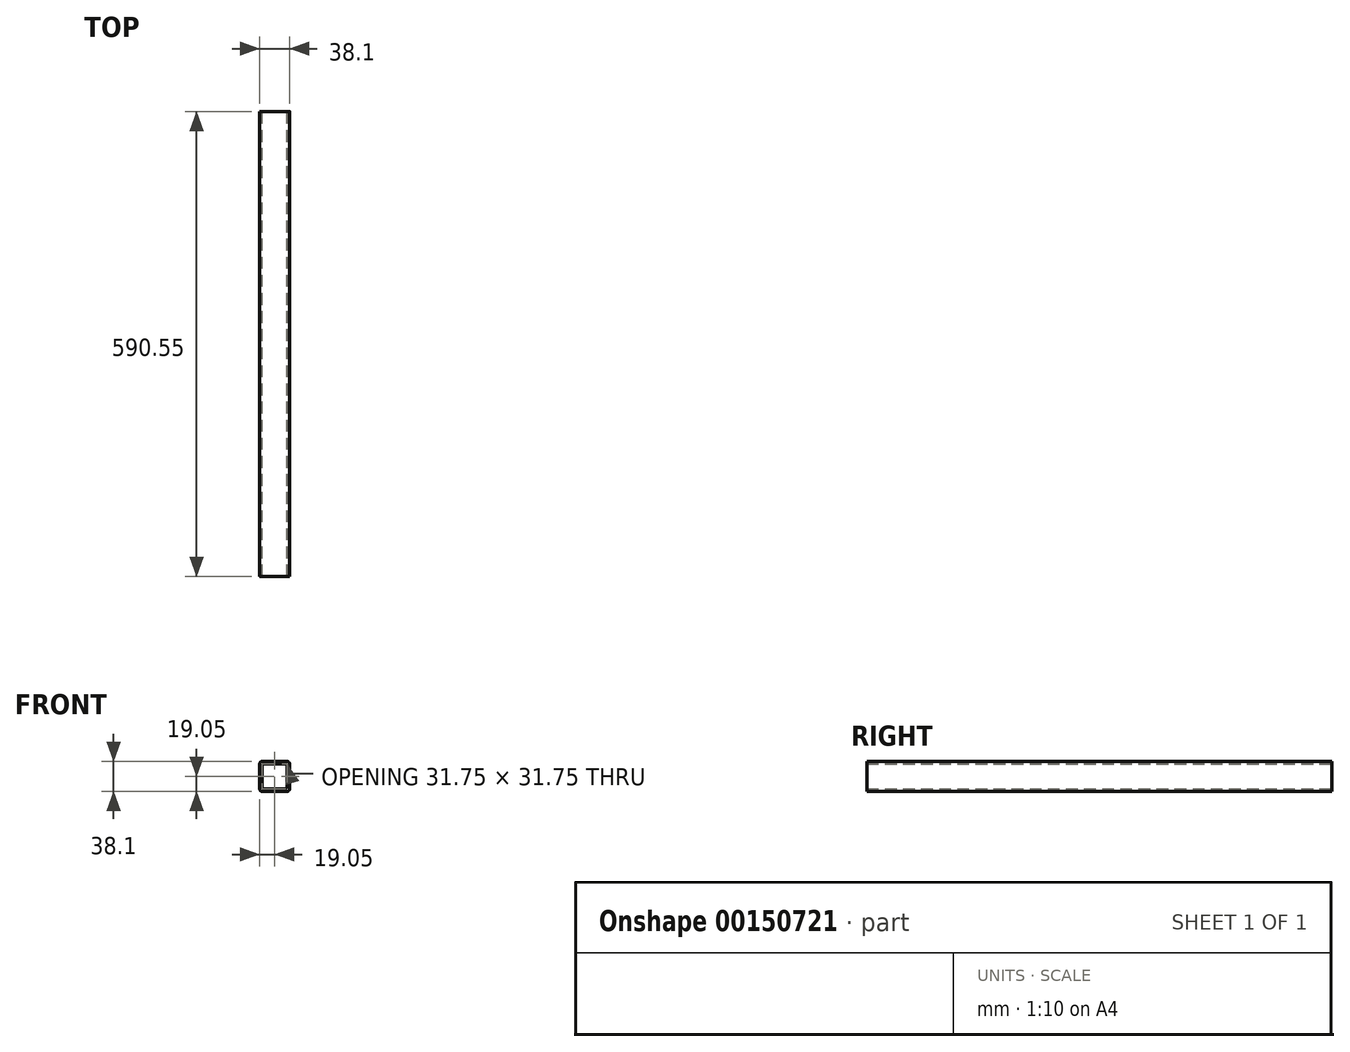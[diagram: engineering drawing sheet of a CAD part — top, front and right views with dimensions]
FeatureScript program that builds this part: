
annotation { "Feature Type Name" : "Feature", "Feature Type Description" : "" }
export const myFeature = defineFeature(function(context is Context, id is Id, definition is map)
    precondition{}
    {
        {
            var Q0;
            Q0=qCreatedBy(makeId("Front.planeOp"),FACE);
            var sketch = newSketch(context, id + "F0", { "sketchPlane" : qUnion([Q0])});
            skLineSegment(sketch, "E0.bottom", {"start": v(15.87, 19.05) * mm, "end": v(-15.87, 19.05) * mm});
            skLineSegment(sketch, "E0.top", {"start": v(15.87, -19.05) * mm, "end": v(-15.87, -19.05) * mm});
            skLineSegment(sketch, "E0.left", {"start": v(19.05, 15.88) * mm, "end": v(19.05, -15.87) * mm});
            skLineSegment(sketch, "E0.right", {"start": v(-19.05, 15.88) * mm, "end": v(-19.05, -15.87) * mm});
            skPoint(sketch, "E0.middle", {"position": v(0, 0) * mm});
            skPoint(sketch, "E1.visualSharp", {"position": v(-19.05, 19.05) * mm});
            skArc(sketch, "E1.filletArc", {"start": v(-15.87, 19.05) * mm, "mid": v(-18.12, 18.12) * mm, "end": v(-19.05, 15.88) * mm});
            skPoint(sketch, "E2.visualSharp", {"position": v(19.05, 19.05) * mm});
            skArc(sketch, "E2.filletArc", {"start": v(19.05, 15.88) * mm, "mid": v(18.12, 18.12) * mm, "end": v(15.87, 19.05) * mm});
            skPoint(sketch, "E3.visualSharp", {"position": v(-19.05, -19.05) * mm});
            skArc(sketch, "E3.filletArc", {"start": v(-19.05, -15.87) * mm, "mid": v(-18.12, -18.12) * mm, "end": v(-15.87, -19.05) * mm});
            skPoint(sketch, "E4.visualSharp", {"position": v(19.05, -19.05) * mm});
            skArc(sketch, "E4.filletArc", {"start": v(15.87, -19.05) * mm, "mid": v(18.12, -18.12) * mm, "end": v(19.05, -15.87) * mm});
            skLineSegment(sketch, "E5.bottom", {"start": v(12.7, 15.88) * mm, "end": v(-12.7, 15.88) * mm});
            skLineSegment(sketch, "E5.top", {"start": v(12.7, -15.88) * mm, "end": v(-12.7, -15.88) * mm});
            skLineSegment(sketch, "E5.left", {"start": v(15.88, 12.7) * mm, "end": v(15.88, -12.7) * mm});
            skLineSegment(sketch, "E5.right", {"start": v(-15.88, 12.7) * mm, "end": v(-15.88, -12.7) * mm});
            skPoint(sketch, "E6.visualSharp", {"position": v(-15.88, 15.87) * mm});
            skArc(sketch, "E6.filletArc", {"start": v(-12.7, 15.88) * mm, "mid": v(-14.95, 14.95) * mm, "end": v(-15.88, 12.7) * mm});
            skPoint(sketch, "E7.visualSharp", {"position": v(15.87, 15.88) * mm});
            skArc(sketch, "E7.filletArc", {"start": v(15.88, 12.7) * mm, "mid": v(14.95, 14.95) * mm, "end": v(12.7, 15.88) * mm});
            skPoint(sketch, "E8.visualSharp", {"position": v(-15.87, -15.88) * mm});
            skArc(sketch, "E8.filletArc", {"start": v(-15.88, -12.7) * mm, "mid": v(-14.95, -14.95) * mm, "end": v(-12.7, -15.88) * mm});
            skPoint(sketch, "E9.visualSharp", {"position": v(15.88, -15.87) * mm});
            skArc(sketch, "E9.filletArc", {"start": v(12.7, -15.88) * mm, "mid": v(14.95, -14.95) * mm, "end": v(15.88, -12.7) * mm});
            skSolve(sketch);
        }
        {
            var Q0;
            Q0 = qSketchRegion(id + "F0", true);
            extrude(context, id + "F1", {"entities" : qUnion([Q0]), "depth" : 590.55 * mm});
        }
    });
